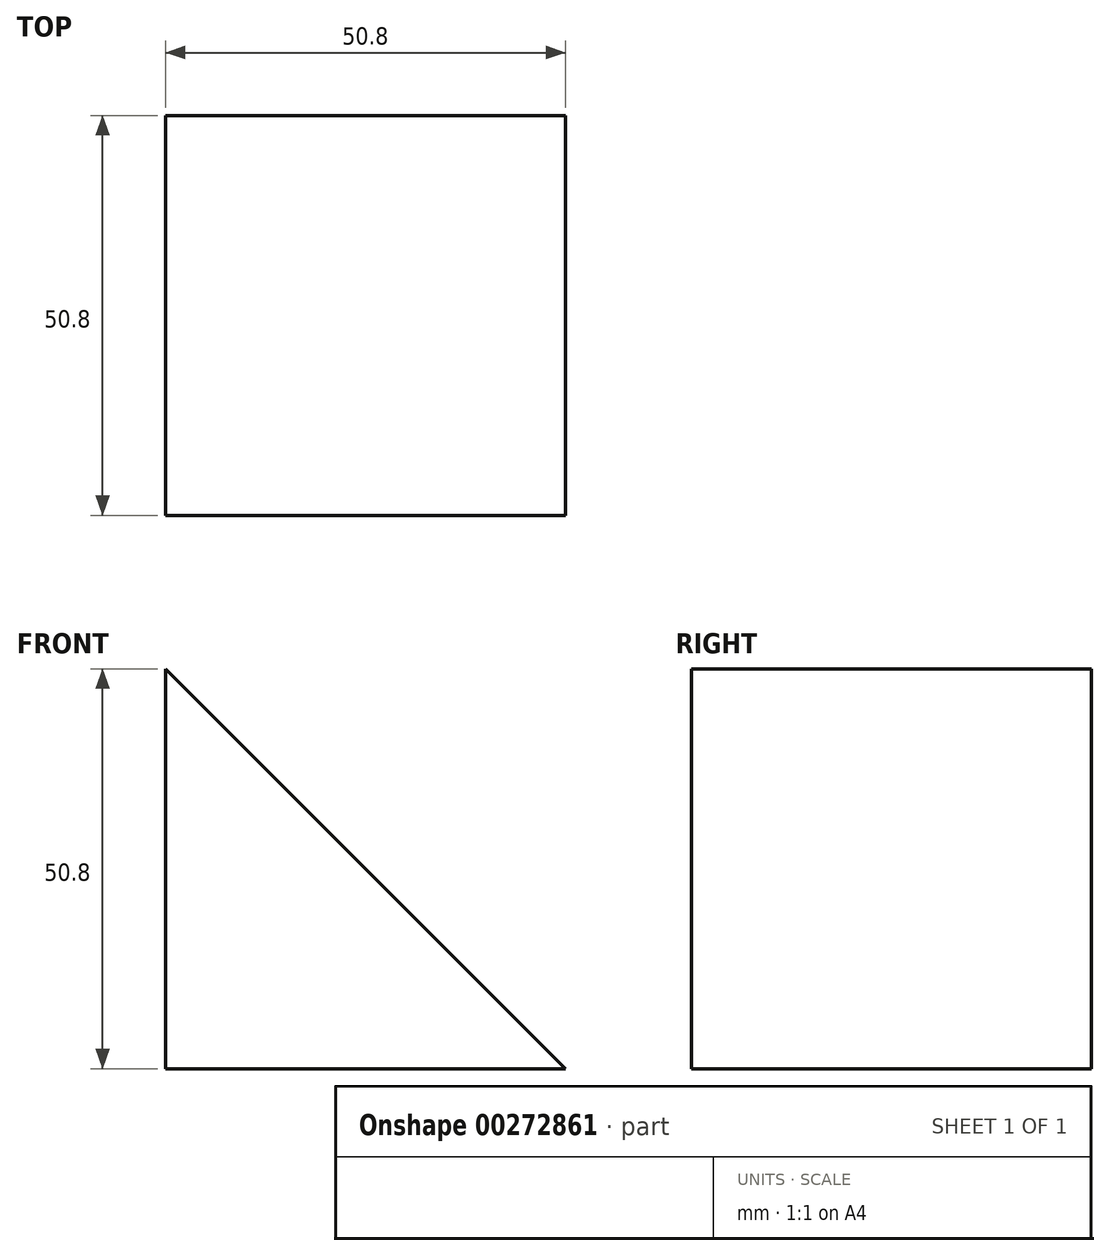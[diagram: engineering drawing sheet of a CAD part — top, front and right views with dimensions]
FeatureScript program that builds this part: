
annotation { "Feature Type Name" : "Feature", "Feature Type Description" : "" }
export const myFeature = defineFeature(function(context is Context, id is Id, definition is map)
    precondition{}
    {
        {
            var Q0;
            Q0=qCreatedBy(makeId("Front.planeOp"),FACE);
            var sketch = newSketch(context, id + "F0", { "sketchPlane" : qUnion([Q0])});
            skLineSegment(sketch, "E0", {"start": v(0, 50.8) * mm, "end": v(0, 0) * mm});
            skLineSegment(sketch, "E1", {"start": v(0, 0) * mm, "end": v(50.8, 0) * mm});
            skLineSegment(sketch, "E2", {"start": v(50.8, 0) * mm, "end": v(0, 50.8) * mm});
            skSolve(sketch);
        }
        {
            var Q0;
            Q0 = qSketchRegion(id + "F0", true);
            extrude(context, id + "F1", {"entities" : qUnion([Q0]), "depth" : 50.8 * mm});
        }
    });
